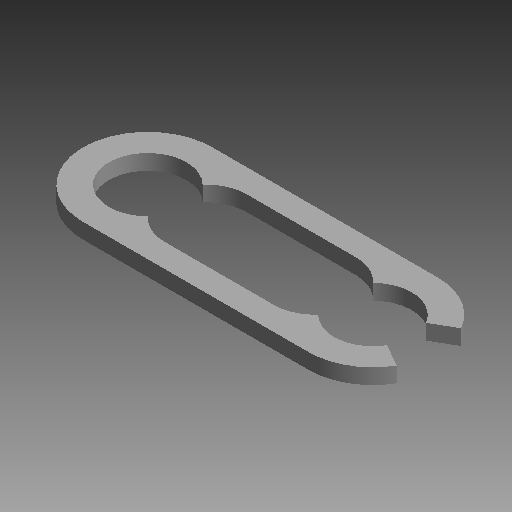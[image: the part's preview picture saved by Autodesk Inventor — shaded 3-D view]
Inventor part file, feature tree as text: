
AUTODESK INVENTOR PART (.ipt)
format: ipt  version: 2019 (Build 230136000, 136)  size: 116,224 bytes
history: native  units: mm (DEFAULTED — no unit token found)
features: other x7, extrude x1, sketch x1
ambient origin geometry x8: Origin, YZ Plane, XZ Plane, XY Plane, X Axis, Y Axis, Z Axis, Center Point
bodies: Solid1 (feature_tree)
feature tree (9):
  extrude  "Extrusion1"  TaperAngle=0.0deg  [1 undecoded]
  other  "clip_XY"
  other  "clip_YZ"
  other  "clip_ZX"
  other  "clip_X"
  other  "clip_Y"
  other  "clip_Z"
  other  "clip_Center"
  sketch  "Sketch_1"  dims[d0=0.65mm d1=0.0mm d2=0.0mm]
note: 1 required parameter value undecoded (feature->parameter linkage not recoverable at this tier; creation-order binding heuristic only, values carry confidence <= 0.55)
